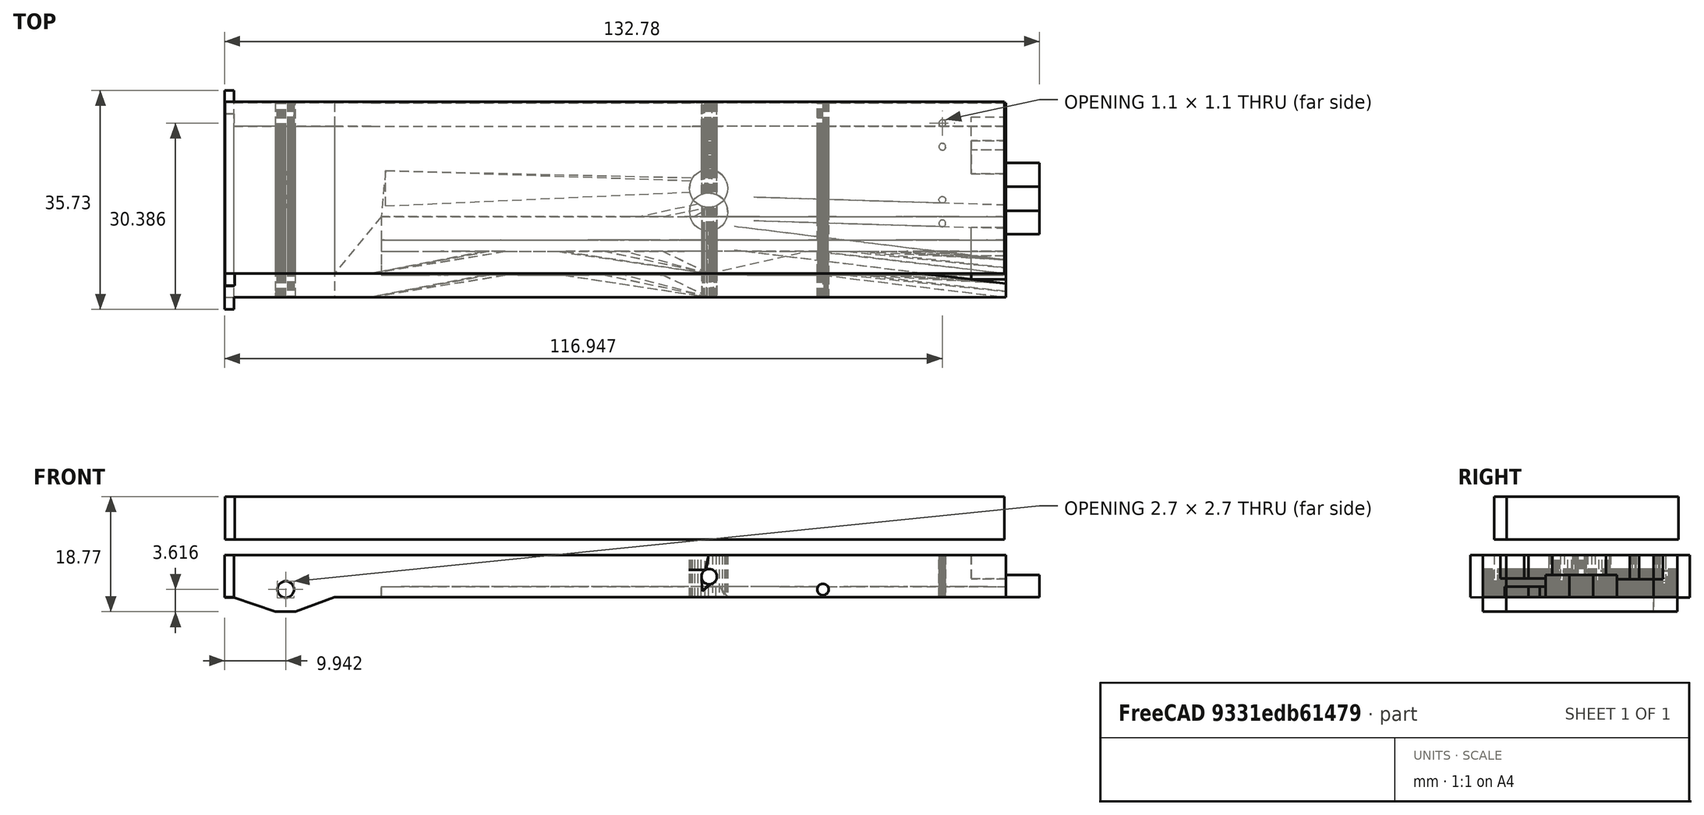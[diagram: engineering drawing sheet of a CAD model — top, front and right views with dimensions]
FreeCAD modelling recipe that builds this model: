
FCSTD DOCUMENT  (FreeCAD 0.16R6712 (Git))
Label: board
License: All rights reserved
LicenseURL: http://en.wikipedia.org/wiki/All_rights_reserved
objects: Part::Feature×3, Sketcher::SketchObject×2, PartDesign::Pad×2, Mesh::Feature×1
note: 9 computed .brp shape members not serialized (recipe doc carries the construction recipe); baked Part::Feature solids carry a one-line shape summary decoded from their .brp

FEATURE [Mesh::Feature] board01
FEATURE [Part::Feature] board01001
  shape: bbox 132.9 x 32 x 9.332 mm, 2627 faces, 0 solids (baked)
FEATURE [Part::Feature] board01001_solid  label="board01001 (Solid)"
  shape: bbox 132.9 x 32 x 9.332 mm, 2627 faces (baked)
FEATURE [Part::Feature] board01001_solid001  label="board01001 (Solid)001"
  Placement = pos=(0,3.855,0) rot=(0,0,1;0rad)
  shape: bbox 132.9 x 32 x 9.332 mm, 1062 faces (baked)
FEATURE [Sketcher::SketchObject] Sketch
  Placement = pos=(0,0,6) rot=(0,0,1;0rad)
  sketch-geometry (4):
    g0: LineSegment StartX=-127.517 StartY=14 StartZ=0 EndX=-0.516974 EndY=14 EndZ=0
    g1: LineSegment StartX=-0.516974 StartY=14 StartZ=0 EndX=-0.516974 EndY=-14 EndZ=0
    g2: LineSegment StartX=-0.516974 StartY=-14 StartZ=0 EndX=-127.517 EndY=-14 EndZ=0
    g3: LineSegment StartX=-127.517 StartY=-14 StartZ=0 EndX=-127.517 EndY=14 EndZ=0
  constraints (10):
    c: Coincident(g0,g1)
    c: Coincident(g1,g2)
    c: Coincident(g2,g3)
    c: Coincident(g3,g0)
    c: Horizontal(g0)
    c: Horizontal(g2)
    c: Vertical(g1)
    c: Vertical(g3)
    c: DistanceY(g3,g3) = 28
    c: DistanceX(g0,g0) = 127
FEATURE [PartDesign::Pad] Pad
  Length = 7
  Length2 = 100
  Placement = pos=(0,0,6) rot=(0,0,1;0rad)
  Sketch = -> Sketch
  Type = 0
FEATURE [Sketcher::SketchObject] Sketch001
  ExternalGeometry = -> [Pad]
  Placement = pos=(0,-14,6) rot=(1,0,0;1.5708rad)
  Support = -> Pad [Face3]
  sketch-geometry (4):
    g0: LineSegment StartX=-127.517 StartY=7 StartZ=0 EndX=-125.938 EndY=7 EndZ=0
    g1: LineSegment StartX=-125.938 StartY=7 StartZ=0 EndX=-125.938 EndY=0 EndZ=0
    g2: LineSegment StartX=-125.938 StartY=0 StartZ=0 EndX=-127.517 EndY=0 EndZ=0
    g3: LineSegment StartX=-127.517 StartY=0 StartZ=0 EndX=-127.517 EndY=7 EndZ=0
  constraints (10):
    c: Coincident(g0,g1)
    c: Coincident(g1,g2)
    c: Coincident(g2,g3)
    c: Coincident(g3,g0)
    c: Horizontal(g0)
    c: Vertical(g1)
    c: Vertical(g3)
    c: Coincident(g0,g-3)
    c: PointOnObject(g1,g-1)
    c: Perpendicular(g-3,g2)
FEATURE [PartDesign::Pad] Pad001
  Length = 2
  Length2 = 100
  Placement = pos=(0,0,6) rot=(0,0,1;0rad)
  Sketch = -> Sketch001
  Type = 0
